# Revit family: Profilschiene- CML3518P2000 FS,FT,A2
name_source: partatom
category: Generic Models
revit_build: Autodesk Revit 2017 (Build: 20190508_0315(x64)
units: mm (PartAtom-declared; Revit-internal decimal feet)

## family parameters
Always vertical = Yes
Can host rebar = No
Cut with Voids When Loaded = No
Part Type = Normal
Room Calculation Point = No
Round Connector Dimension = Use Diameter
Shared = No
Work Plane-Based = No

## types (3) — shared parameters
Cut's number = 40
Cut's space = 50 mm  [stored 0.164042 ft]
Length = 2000 mm  [stored 6.56168 ft]
Manufacturer = OBO Bettermann
URL = http://www.obo-bettermann.com
Width = 35 mm
Width 1 = 18 mm

## per-type parameters (varying)
| type | GTIN | Manufacturer Art.No. | Material |
| CML3518P2000FS | 4012195038771 | 1104500 | Strip-galvanised |
| CML3518P2000FT | 4012196470938 | 1104570 | Hot-dip galvanised |
| CML3518P2000A2 | 4012195627081 | 1104501 | Stainless steel, A2 |

note: column(s) folded — value = type name in every type: Article Type

note: [stored X ft] marks values corroborated as IEEE doubles in the binary element streams (Revit-internal decimal feet)

## geometry (parser evidence)
native form markers: Sweep x2
no freeform markers — native parametric forms only
